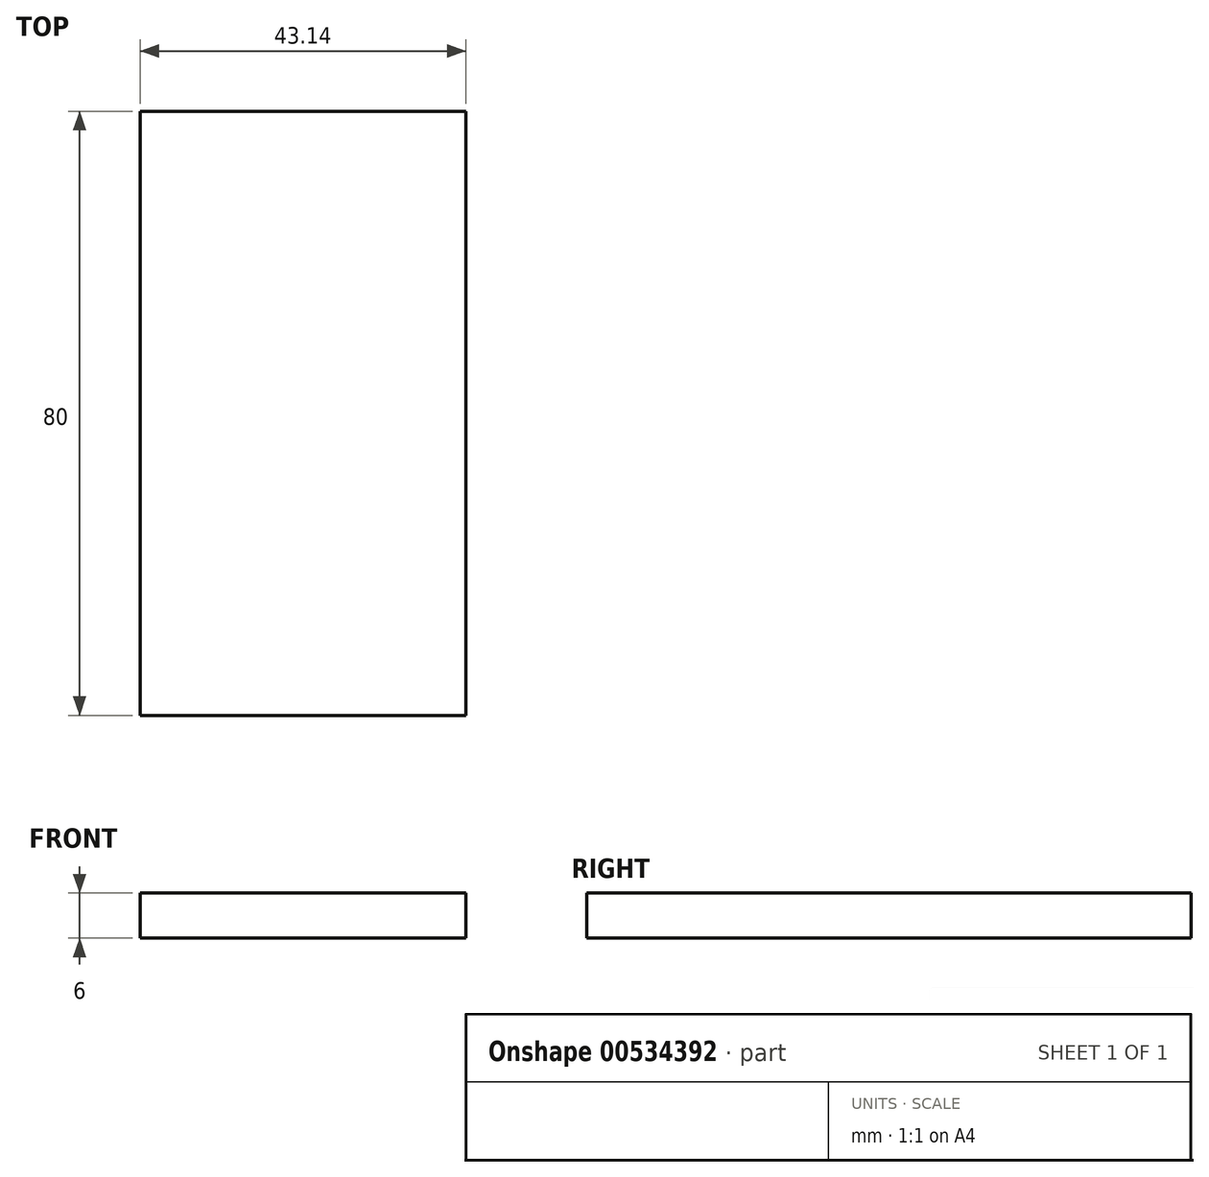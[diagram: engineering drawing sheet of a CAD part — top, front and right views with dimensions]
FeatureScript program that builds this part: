
annotation { "Feature Type Name" : "Feature", "Feature Type Description" : "" }
export const myFeature = defineFeature(function(context is Context, id is Id, definition is map)
    precondition{}
    {
        {
            var Q0;
            Q0=qCreatedBy(makeId("Top.planeOp"),FACE);
            var sketch = newSketch(context, id + "F0", { "sketchPlane" : qUnion([Q0])});
            skLineSegment(sketch, "E0.bottom", {"start": v(21.57, 40) * mm, "end": v(-21.57, 40) * mm});
            skLineSegment(sketch, "E0.top", {"start": v(21.57, -40) * mm, "end": v(-21.57, -40) * mm});
            skLineSegment(sketch, "E0.left", {"start": v(21.57, 40) * mm, "end": v(21.57, -40) * mm});
            skLineSegment(sketch, "E0.right", {"start": v(-21.57, 40) * mm, "end": v(-21.57, -40) * mm});
            skPoint(sketch, "E0.middle", {"position": v(0, 0) * mm});
            skSolve(sketch);
        }
        {
            var Q0;
            Q0 = qSketchRegion(id + "F0", true);
            extrude(context, id + "F1", {"entities" : qUnion([Q0]), "depth" : 6 * mm, "offsetDistance" : 25 * mm});
        }
    });
